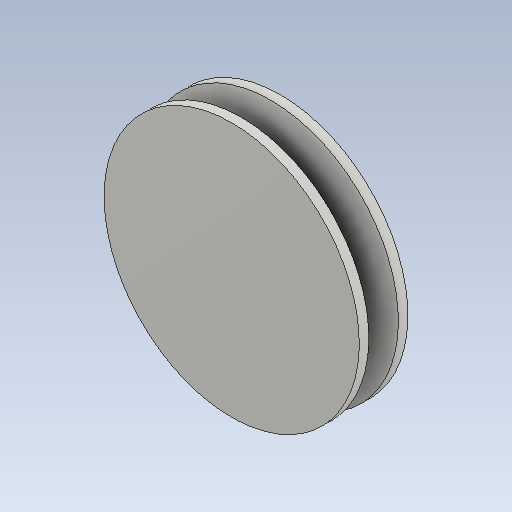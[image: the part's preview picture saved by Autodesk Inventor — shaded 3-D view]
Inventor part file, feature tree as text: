
AUTODESK INVENTOR PART (.ipt)
format: ipt  version: 2020.5 (Build 245400000, 400)  size: 130,048 bytes
history: native  units: mm (DEFAULTED — no unit token found)
features: other x3, fillet x2, sketch x1, pattern_linear x1
ambient origin geometry x8: Origin, YZ Plane, XZ Plane, XY Plane, X Axis, Y Axis, Z Axis, Center Point
bodies: Solid1 (feature_tree)
feature tree (7):
  sketch  "Boceto principal"  dims[d2=2.0mm d5=8.0mm d6=16.0mm d7=90.0deg d8=0.0mm d9=0.0mm d10=0.0mm d11=0.0mm d15=90.0deg d16=10.0mm d18=12.0mm d21=80.0mm d24=0.0mm d25=11.0mm d26=0.0mm d27=8.0mm]
  other  "Plano de correa"
  other  "Cuerpo"
  other  "Para ranuras"
  fillet  "Empalme externo"  Radius=8.5mm
  fillet  "Empalme interno"  Radius=5.934119mm
  pattern_linear  "Patrón para ranuras"  Spacing1=8.0mm  [1 undecoded]
note: 1 required parameter value undecoded (feature->parameter linkage not recoverable at this tier; creation-order binding heuristic only, values carry confidence <= 0.55)
